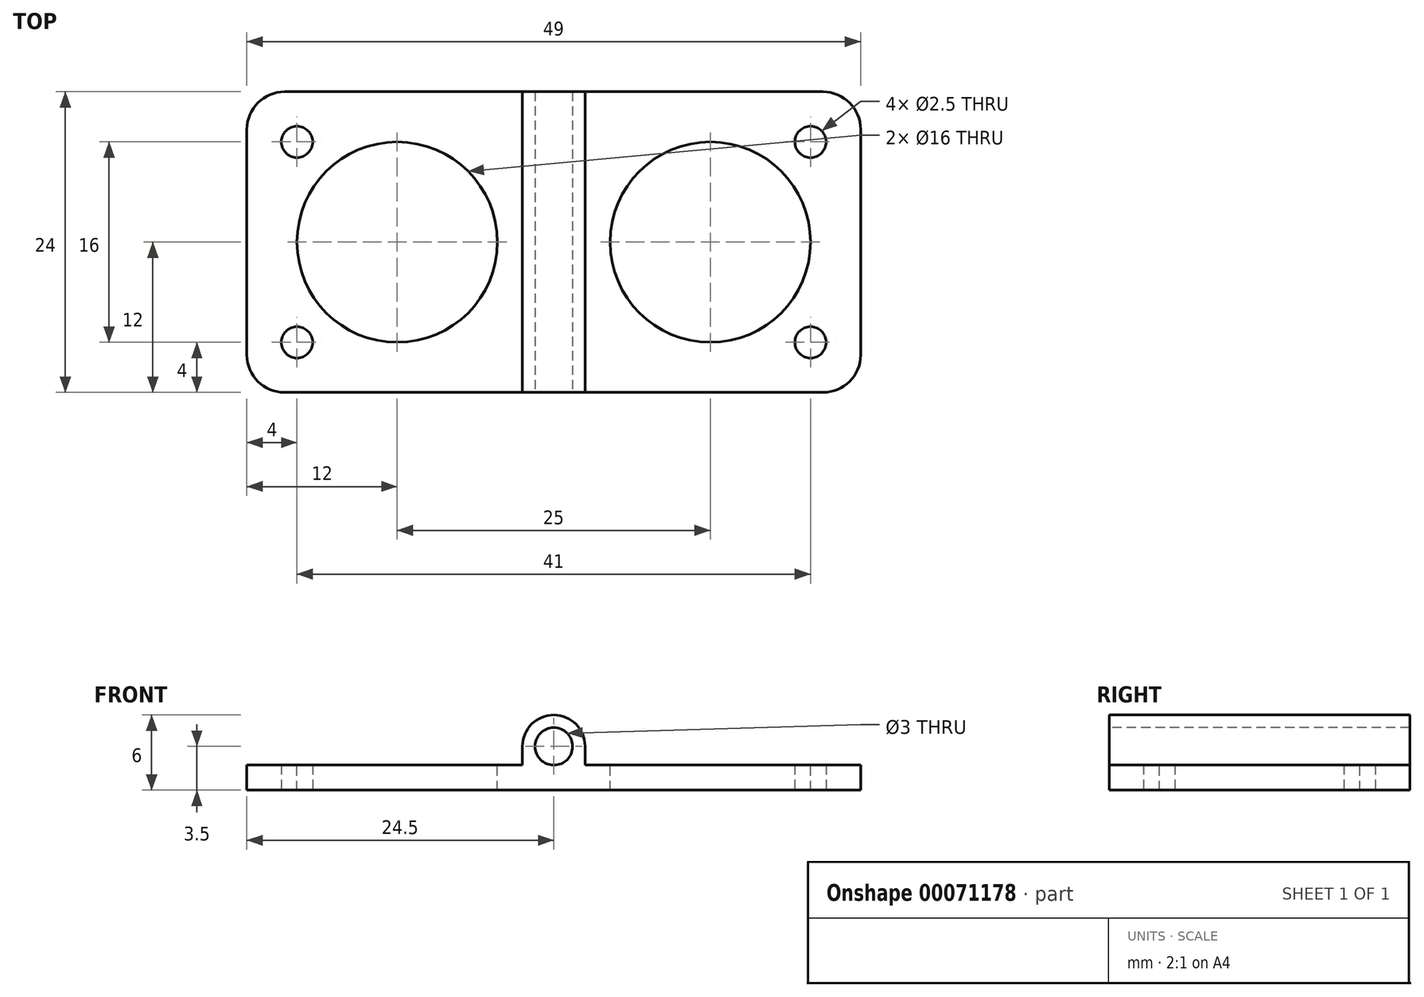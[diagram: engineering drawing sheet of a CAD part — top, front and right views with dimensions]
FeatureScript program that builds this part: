
annotation { "Feature Type Name" : "Feature", "Feature Type Description" : "" }
export const myFeature = defineFeature(function(context is Context, id is Id, definition is map)
    precondition{}
    {
        {
            var Q0;
            Q0=qCreatedBy(makeId("Top.planeOp"),FACE);
            var sketch = newSketch(context, id + "F0", { "sketchPlane" : qUnion([Q0])});
            skLineSegment(sketch, "E0.bottom", {"start": v(0, 0) * mm, "end": v(-45, 0) * mm});
            skLineSegment(sketch, "E0.top", {"start": v(0, 20) * mm, "end": v(-45, 20) * mm});
            skLineSegment(sketch, "E0.left", {"start": v(0, 0) * mm, "end": v(0, 20) * mm});
            skLineSegment(sketch, "E0.right", {"start": v(-45, 0) * mm, "end": v(-45, 20) * mm});
            skSolve(sketch);
        }
        {
            var Q0;
            Q0=qCreatedBy(makeId("Top.planeOp"),FACE);
            var sketch = newSketch(context, id + "F1", { "sketchPlane" : qUnion([Q0])});
            skLineSegment(sketch, "E1.bottom", {"start": v(-47, 22) * mm, "end": v(2, 22) * mm});
            skLineSegment(sketch, "E1.top", {"start": v(-47, -2) * mm, "end": v(2, -2) * mm});
            skLineSegment(sketch, "E1.left", {"start": v(-47, 22) * mm, "end": v(-47, -2) * mm});
            skLineSegment(sketch, "E1.right", {"start": v(2, 22) * mm, "end": v(2, -2) * mm});
            skPoint(sketch, "E2", {"position": v(-43, 18) * mm});
            skPoint(sketch, "E3", {"position": v(-43, 2) * mm});
            skPoint(sketch, "E4", {"position": v(-2, 2) * mm});
            skPoint(sketch, "E5", {"position": v(-2, 18) * mm});
            skCircle(sketch, "E6", {"center": v(-43, 18) * mm, "radius": 1.25 * mm});
            skCircle(sketch, "E7", {"center": v(-43, 2) * mm, "radius": 1.25 * mm});
            skCircle(sketch, "E8", {"center": v(-2, 2) * mm, "radius": 1.25 * mm});
            skCircle(sketch, "E9", {"center": v(-2, 18) * mm, "radius": 1.25 * mm});
            skSolve(sketch);
        }
        {
            var Q0;
            Q0 = qSketchRegion(id + "F1", true);
            extrude(context, id + "F2", {"entities" : qUnion([Q0]), "depth" : 2 * mm});
        }
        {
            var Q0;
            Q0=makeQuery(id+"F2.opExtrude","CAP_FACE",FACE,{"disambiguationData":[OSD([sQuery(id+"F1.wireOp",EDGE,"E1.bottom"),sQuery(id+"F1.wireOp",EDGE,"E1.top"),sQuery(id+"F1.wireOp",EDGE,"E1.left"),sQuery(id+"F1.wireOp",EDGE,"E1.right"),sQuery(id+"F1.wireOp",EDGE,"E6"),sQuery(id+"F1.wireOp",EDGE,"E7"),sQuery(id+"F1.wireOp",EDGE,"E8"),sQuery(id+"F1.wireOp",EDGE,"E9")])],"isStart":false});
            var sketch = newSketch(context, id + "F3", { "sketchPlane" : qUnion([Q0])});
            skLineSegment(sketch, "E10.bottom", {"start": v(-25, 22) * mm, "end": v(-20, 22) * mm});
            skLineSegment(sketch, "E10.top", {"start": v(-25, -2) * mm, "end": v(-20, -2) * mm});
            skLineSegment(sketch, "E10.left", {"start": v(-25, 22) * mm, "end": v(-25, -2) * mm});
            skLineSegment(sketch, "E10.right", {"start": v(-20, 22) * mm, "end": v(-20, -2) * mm});
            skPoint(sketch, "E11", {"position": v(-22.5, 22) * mm});
            skSolve(sketch);
        }
        {
            var Q0;
            Q0 = qSketchRegion(id + "F3", true);
            extrude(context, id + "F4", {"entities" : qUnion([Q0]), "operationType" : NewBodyOperationType.ADD, "depth" : 4 * mm});
        }
        {
            var Q0;
            Q0=makeQuery(id+"F4.boolean.opBoolean","MERGE",FACE,{"derivedFrom":[makeQuery(id+"F2.opExtrude","SWEPT_FACE",FACE,{"disambiguationData":[OSD([sQuery(id+"F1.wireOp",EDGE,"E1.top")])]}),makeQuery(id+"F4.opExtrude","SWEPT_FACE",FACE,{"disambiguationData":[OSD([sQuery(id+"F3.wireOp",EDGE,"E10.top")])]})]});
            var sketch = newSketch(context, id + "F5", { "sketchPlane" : qUnion([Q0])});
            skPoint(sketch, "E12", {"position": v(-25, 4) * mm});
            skPoint(sketch, "E13", {"position": v(-22.5, 6) * mm});
            skCircle(sketch, "E14", {"center": v(-22.5, 3.5) * mm, "radius": 1.5 * mm});
            skSolve(sketch);
        }
        {
            var Q0;
            Q0 = qSketchRegion(id + "F5", true);
            var Q1;
            Q1=makeQuery(id+"F4.boolean.opBoolean","MERGE",FACE,{"derivedFrom":[makeQuery(id+"F2.opExtrude","SWEPT_FACE",FACE,{"disambiguationData":[OSD([sQuery(id+"F1.wireOp",EDGE,"E1.bottom")])]}),makeQuery(id+"F4.opExtrude","SWEPT_FACE",FACE,{"disambiguationData":[OSD([sQuery(id+"F3.wireOp",EDGE,"E10.bottom")])]})]});
            extrude(context, id + "F6", {"entities" : qUnion([Q0]), "operationType" : NewBodyOperationType.REMOVE, "endBound" : BoundingType.UP_TO_SURFACE, "oppositeDirection" : true, "endBoundEntityFace" : qUnion([Q1]), "depth" : 25 * mm});
        }
        {
            var Q0;
            Q0=makeQuery(id+"F4.opExtrude","CAP_EDGE",EDGE,{"disambiguationData":[OSD([sQuery(id+"F3.wireOp",EDGE,"E10.right")])],"isStart":false});
            var Q1;
            Q1=makeQuery(id+"F4.opExtrude","CAP_EDGE",EDGE,{"disambiguationData":[OSD([sQuery(id+"F3.wireOp",EDGE,"E10.left")])],"isStart":false});
            fillet(context, id + "F7", {"entities" : qUnion([Q0, Q1]), "radius" : 2.5 * mm, "tangentPropagation" : true, "allowEdgeOverflow" : false});
        }
        {
            var Q0;
            Q0=makeQuery(id+"F2.opExtrude","SWEPT_EDGE",EDGE,{"disambiguationData":[OSD([sQuery(id+"F1.wireOp",EDGE,"E1.top"),sQuery(id+"F1.wireOp",EDGE,"E1.right")])]});
            var Q1;
            Q1=makeQuery(id+"F2.opExtrude","SWEPT_EDGE",EDGE,{"disambiguationData":[OSD([sQuery(id+"F1.wireOp",EDGE,"E1.bottom"),sQuery(id+"F1.wireOp",EDGE,"E1.right")])]});
            var Q2;
            Q2=makeQuery(id+"F2.opExtrude","SWEPT_EDGE",EDGE,{"disambiguationData":[OSD([sQuery(id+"F1.wireOp",EDGE,"E1.bottom"),sQuery(id+"F1.wireOp",EDGE,"E1.left")])]});
            var Q3;
            Q3=makeQuery(id+"F2.opExtrude","SWEPT_EDGE",EDGE,{"disambiguationData":[OSD([sQuery(id+"F1.wireOp",EDGE,"E1.top"),sQuery(id+"F1.wireOp",EDGE,"E1.left")])]});
            fillet(context, id + "F8", {"entities" : qUnion([Q0, Q1, Q2, Q3]), "radius" : 3 * mm, "tangentPropagation" : true, "allowEdgeOverflow" : false});
        }
        {
            var Q0;
            {var subQ0=sQuery(id+"F1.wireOp",EDGE,"E6");var subQ1=sQuery(id+"F1.wireOp",EDGE,"E1.left");var subQ2=sQuery(id+"F1.wireOp",EDGE,"E1.top");var subQ3=sQuery(id+"F1.wireOp",EDGE,"E1.bottom");var subQ4=sQuery(id+"F1.wireOp",EDGE,"E7");Q0=makeQuery(id+"F4.boolean.opBoolean","SPLIT",FACE,{"disambiguationData":[TD([makeQuery(id+"F2.opExtrude","SWEPT_FACE",FACE,{"disambiguationData":[OSD([subQ1])]})])],"derivedFrom":makeQuery(id+"F2.opExtrude","CAP_FACE",FACE,{"disambiguationData":[OSD([subQ3,subQ2,subQ1,sQuery(id+"F1.wireOp",EDGE,"E1.right"),subQ0,subQ4,sQuery(id+"F1.wireOp",EDGE,"E8"),sQuery(id+"F1.wireOp",EDGE,"E9")])],"isStart":false})});}
            var sketch = newSketch(context, id + "F9", { "sketchPlane" : qUnion([Q0])});
            skCircle(sketch, "E15", {"center": v(-35, 10) * mm, "radius": 8 * mm});
            skCircle(sketch, "E16", {"center": v(-10, 10) * mm, "radius": 8 * mm});
            skLineSegment(sketch, "E17", {"start": v(-35, 10) * mm, "end": v(-10, 10) * mm, "construction": true});
            skPoint(sketch, "E18", {"position": v(-22.5, 10) * mm});
            skPoint(sketch, "E19", {"position": v(-22.5, 22) * mm});
            skPoint(sketch, "E20", {"position": v(-47, 10) * mm});
            skSolve(sketch);
        }
        {
            var Q0;
            Q0 = qSketchRegion(id + "F9", true);
            var Q1;
            Q1=makeQuery(id+"F2.opExtrude","CAP_FACE",FACE,{"disambiguationData":[OSD([sQuery(id+"F1.wireOp",EDGE,"E1.bottom"),sQuery(id+"F1.wireOp",EDGE,"E1.top"),sQuery(id+"F1.wireOp",EDGE,"E1.left"),sQuery(id+"F1.wireOp",EDGE,"E1.right"),sQuery(id+"F1.wireOp",EDGE,"E6"),sQuery(id+"F1.wireOp",EDGE,"E7"),sQuery(id+"F1.wireOp",EDGE,"E8"),sQuery(id+"F1.wireOp",EDGE,"E9")])],"isStart":true});
            extrude(context, id + "F10", {"entities" : qUnion([Q0]), "operationType" : NewBodyOperationType.REMOVE, "endBound" : BoundingType.UP_TO_SURFACE, "oppositeDirection" : true, "endBoundEntityFace" : qUnion([Q1]), "depth" : 25 * mm});
        }
    });
